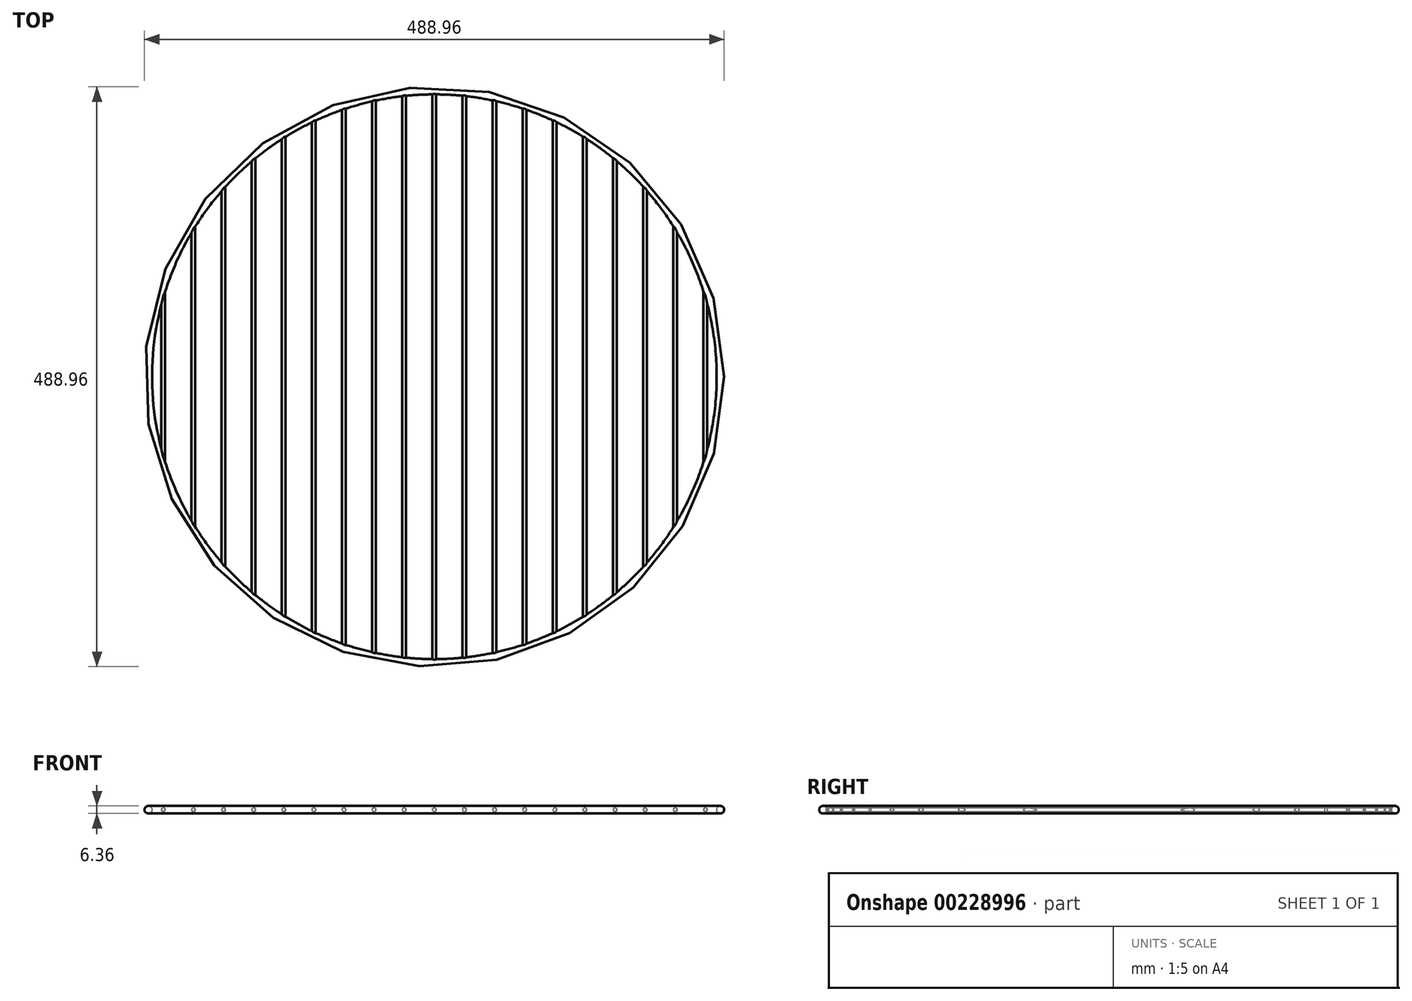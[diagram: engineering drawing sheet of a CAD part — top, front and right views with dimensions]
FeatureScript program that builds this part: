
annotation { "Feature Type Name" : "Feature", "Feature Type Description" : "" }
export const myFeature = defineFeature(function(context is Context, id is Id, definition is map)
    precondition{}
    {
        {
            var Q0;
            Q0=qCreatedBy(makeId("Front.planeOp"),FACE);
            var sketch = newSketch(context, id + "F0", { "sketchPlane" : qUnion([Q0])});
            skCircle(sketch, "E0", {"center": v(241.3, 0) * mm, "radius": 3.18 * mm});
            skLineSegment(sketch, "E1", {"start": v(0, 0) * mm, "end": v(0, 32.12) * mm, "construction": true});
            skSolve(sketch);
        }
        {
            var Q0;
            Q0=qCreatedBy(makeId("Front.planeOp"),FACE);
            var sketch = newSketch(context, id + "F1", { "sketchPlane" : qUnion([Q0])});
            skCircle(sketch, "E2", {"center": v(0, 0) * mm, "radius": 1.59 * mm});
            skCircle(sketch, "E3.1.0.0", {"center": v(25.4, 0) * mm, "radius": 1.59 * mm});
            skCircle(sketch, "E3.2.0.0", {"center": v(50.8, 0) * mm, "radius": 1.59 * mm});
            skCircle(sketch, "E3.3.0.0", {"center": v(76.2, 0) * mm, "radius": 1.59 * mm});
            skCircle(sketch, "E3.4.0.0", {"center": v(101.6, 0) * mm, "radius": 1.59 * mm});
            skCircle(sketch, "E3.5.0.0", {"center": v(127, 0) * mm, "radius": 1.59 * mm});
            skCircle(sketch, "E3.6.0.0", {"center": v(152.4, 0) * mm, "radius": 1.59 * mm});
            skCircle(sketch, "E3.7.0.0", {"center": v(177.8, 0) * mm, "radius": 1.59 * mm});
            skCircle(sketch, "E3.8.0.0", {"center": v(203.2, 0) * mm, "radius": 1.59 * mm});
            skCircle(sketch, "E3.9.0.0", {"center": v(228.6, 0) * mm, "radius": 1.59 * mm});
            skLineSegment(sketch, "E3.direction1", {"start": v(0, 0) * mm, "end": v(25.4, 0) * mm, "construction": true});
            skCircle(sketch, "E4.1.0.0", {"center": v(-25.4, 0) * mm, "radius": 1.59 * mm});
            skCircle(sketch, "E4.2.0.0", {"center": v(-50.8, 0) * mm, "radius": 1.59 * mm});
            skCircle(sketch, "E4.3.0.0", {"center": v(-76.2, 0) * mm, "radius": 1.59 * mm});
            skCircle(sketch, "E4.4.0.0", {"center": v(-101.6, 0) * mm, "radius": 1.59 * mm});
            skCircle(sketch, "E4.5.0.0", {"center": v(-127, 0) * mm, "radius": 1.59 * mm});
            skCircle(sketch, "E4.6.0.0", {"center": v(-152.4, 0) * mm, "radius": 1.59 * mm});
            skCircle(sketch, "E4.7.0.0", {"center": v(-177.8, 0) * mm, "radius": 1.59 * mm});
            skCircle(sketch, "E4.8.0.0", {"center": v(-203.2, 0) * mm, "radius": 1.59 * mm});
            skCircle(sketch, "E4.9.0.0", {"center": v(-228.6, 0) * mm, "radius": 1.59 * mm});
            skLineSegment(sketch, "E4.direction1", {"start": v(0, 0) * mm, "end": v(-25.4, 0) * mm, "construction": true});
            skSolve(sketch);
        }
        {
            var Q0;
            Q0=makeQuery(id+"F0.imprint","IMPRINT",FACE,{"disambiguationData":[TD([[makeQuery(id+"F0.imprint","IMPRINT",EDGE,{"derivedFrom":sQuery(id+"F0.wireOp",EDGE,"E0")}),1.0]])]});
            var Q1;
            Q1=sQuery(id+"F0.wireOp",EDGE,"E1");
            revolve(context, id + "F2", {"entities" : qUnion([Q0]), "axis" : qUnion([Q1]), "revolveType" : RevolveType.FULL});
        }
        {
            var Q0;
            Q0 = qSketchRegion(id + "F1", true);
            extrude(context, id + "F3", {"entities" : qUnion([Q0]), "operationType" : NewBodyOperationType.ADD, "endBound" : BoundingType.UP_TO_NEXT, "depth" : 25.4 * mm, "hasSecondDirection" : true, "secondDirectionBound" : SecondDirectionBoundingType.UP_TO_NEXT, "secondDirectionOppositeDirection" : true, "secondDirectionDepth" : 25.4 * mm});
        }
    });
